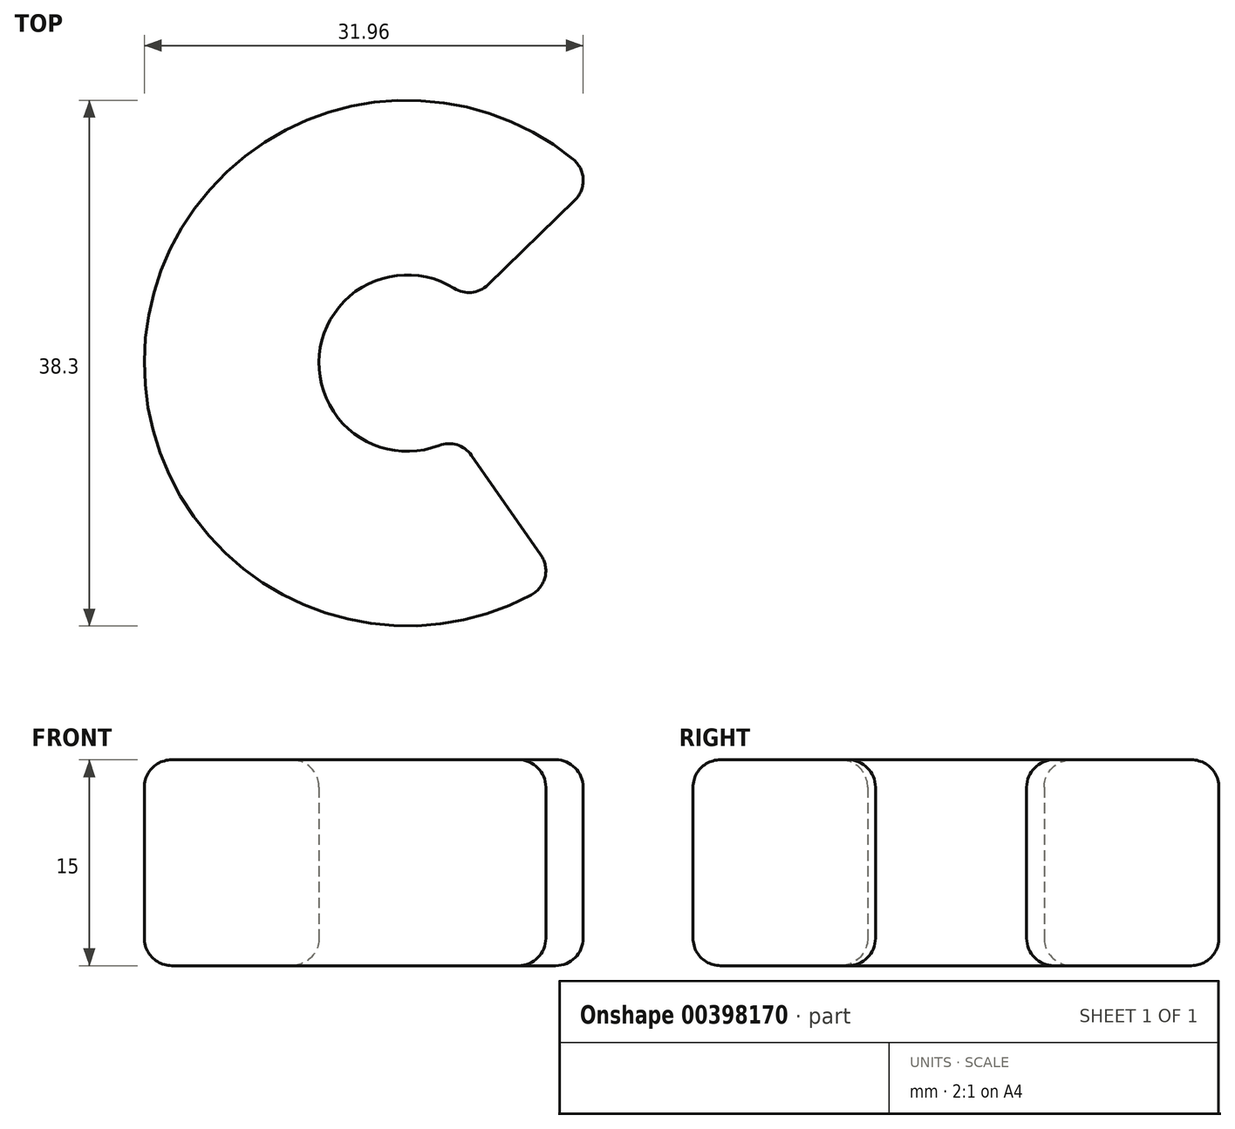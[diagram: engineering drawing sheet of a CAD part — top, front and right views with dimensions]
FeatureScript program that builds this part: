
annotation { "Feature Type Name" : "Feature", "Feature Type Description" : "" }
export const myFeature = defineFeature(function(context is Context, id is Id, definition is map)
    precondition{}
    {
        {
            var Q0;
            Q0=qCreatedBy(makeId("Top.planeOp"),FACE);
            var sketch = newSketch(context, id + "F0", { "sketchPlane" : qUnion([Q0])});
            skCircle(sketch, "E0", {"center": v(0, 0) * mm, "radius": 19.15 * mm});
            skCircle(sketch, "E1", {"center": v(0, 0) * mm, "radius": 6.43 * mm});
            skLineSegment(sketch, "E2", {"start": v(0, 0) * mm, "end": v(13.72, 13.35) * mm});
            skLineSegment(sketch, "E3", {"start": v(0, 0) * mm, "end": v(11.68, -16.77) * mm});
            skSolve(sketch);
        }
        {
            var Q0;
            {var subQ0=sQuery(id+"F0.wireOp",EDGE,"E2");var subQ1=sQuery(id+"F0.wireOp",EDGE,"E0");var subQ2=makeQuery(id+"F0.imprint","INTERSECT",VERTEX,{"derivedFrom":[subQ1,subQ0]});Q0=makeQuery(id+"F0.imprint","IMPRINT",FACE,{"disambiguationData":[TD([[makeQuery(id+"F0.imprint","IMPRINT",EDGE,{"disambiguationData":[TD([[subQ2,-1.0]])],"derivedFrom":subQ1}),1.0]])]});}
            extrude(context, id + "F1", {"entities" : qUnion([Q0]), "depth" : 15 * mm});
        }
        {
            var Q0;
            Q0=makeQuery(id+"F1.opExtrude","CAP_FACE",FACE,{"disambiguationData":[OSD([sQuery(id+"F0.wireOp",EDGE,"E0"),sQuery(id+"F0.wireOp",EDGE,"E1"),sQuery(id+"F0.wireOp",EDGE,"E2"),sQuery(id+"F0.wireOp",EDGE,"E3")])],"isStart":false});
            var Q1;
            Q1=makeQuery(id+"F1.opExtrude","CAP_EDGE",EDGE,{"disambiguationData":[OSD([sQuery(id+"F0.wireOp",EDGE,"E0")])],"isStart":true});
            var Q2;
            Q2=makeQuery(id+"F1.opExtrude","SWEPT_FACE",FACE,{"disambiguationData":[OSD([sQuery(id+"F0.wireOp",EDGE,"E3")])]});
            var Q3;
            Q3=makeQuery(id+"F1.opExtrude","SWEPT_FACE",FACE,{"disambiguationData":[OSD([sQuery(id+"F0.wireOp",EDGE,"E2")])]});
            var Q4;
            Q4=makeQuery(id+"F1.opExtrude","SWEPT_FACE",FACE,{"disambiguationData":[OSD([sQuery(id+"F0.wireOp",EDGE,"E1")])]});
            var Q5;
            Q5=makeQuery(id+"F1.opExtrude","SWEPT_FACE",FACE,{"disambiguationData":[OSD([sQuery(id+"F0.wireOp",EDGE,"E0")])]});
            fillet(context, id + "F2", {"entities" : qUnion([Q0, Q1, Q2, Q3, Q4, Q5]), "radius" : 2 * mm, "tangentPropagation" : true, "allowEdgeOverflow" : false});
        }
    });
